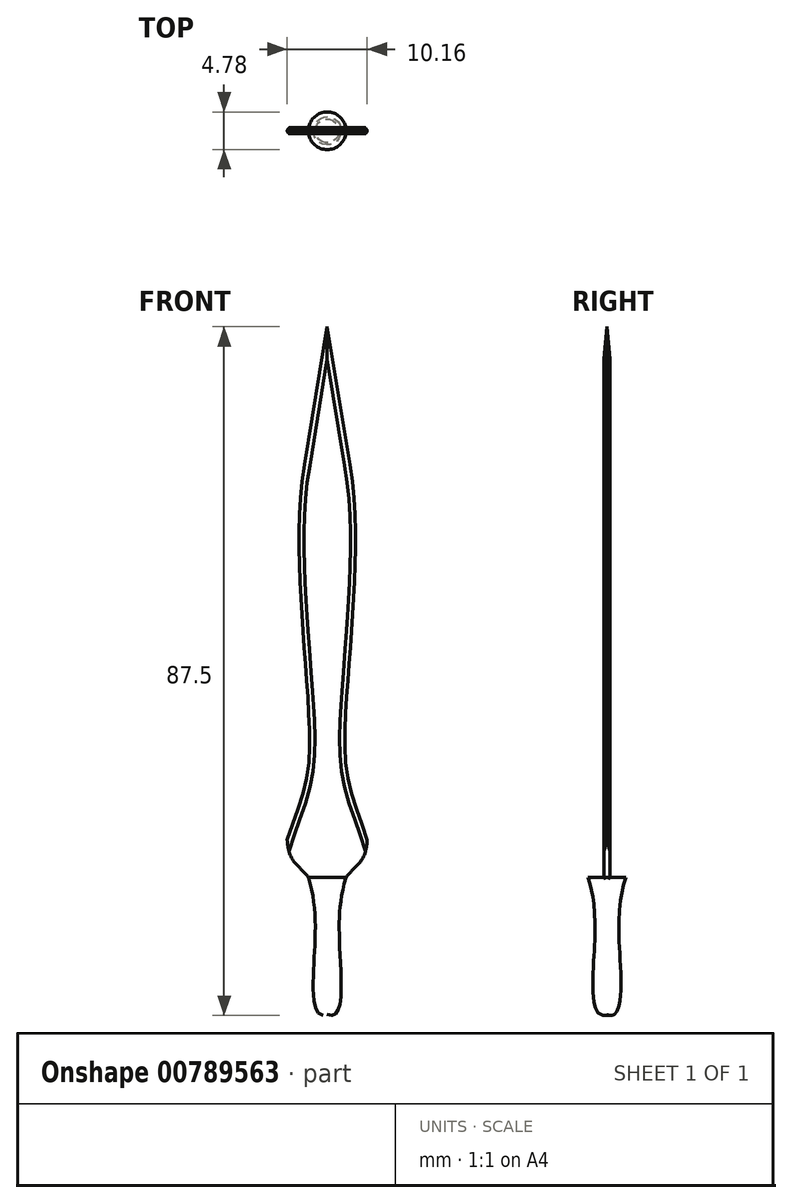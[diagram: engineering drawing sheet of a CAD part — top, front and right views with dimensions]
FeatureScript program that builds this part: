
annotation { "Feature Type Name" : "Feature", "Feature Type Description" : "" }
export const myFeature = defineFeature(function(context is Context, id is Id, definition is map)
    precondition{}
    {
        {
            var Q0;
            Q0=qCreatedBy(makeId("Front.planeOp"),FACE);
            var sketch = newSketch(context, id + "F0", { "sketchPlane" : qUnion([Q0])});
            skLineSegment(sketch, "E0", {"start": v(0, -22.19) * mm, "end": v(0, 65.19) * mm});
            skPoint(sketch, "E1", {"position": v(0, 0) * mm});
            skLineSegment(sketch, "E2", {"start": v(0, 65.19) * mm, "end": v(2.86, 47.67) * mm});
            skPoint(sketch, "E3", {"position": v(1.62, -18.97) * mm});
            skPoint(sketch, "E4", {"position": v(5.08, 0) * mm});
            skFitSpline(sketch, "E5", {"points": [v(2.86, 47.67) * mm, v(2.26, 11.25) * mm, v(5.08, 0) * mm], "startDerivative": vector(9.57, -51.1) * mm, "endDerivative": vector(12.53, -39.06) * mm});
            skFitSpline(sketch, "E6", {"points": [v(5.08, 0) * mm, v(2.23, -5.07) * mm, v(1.62, -18.97) * mm, v(0, -22.19) * mm], "startDerivative": vector(-1.76, -33.31) * mm, "endDerivative": vector(-17, 3.2) * mm});
            skLineSegment(sketch, "E7.MirrorCS", {"start": v(0, 65.19) * mm, "end": v(-2.86, 47.67) * mm});
            skFitSpline(sketch, "E8.MirrorCS", {"points": [v(-2.86, 47.67) * mm, v(-2.26, 11.25) * mm, v(-5.08, 0) * mm], "startDerivative": vector(-9.57, -51.1) * mm, "endDerivative": vector(-12.53, -39.06) * mm});
            skFitSpline(sketch, "E9.MirrorCS", {"points": [v(-5.08, 0) * mm, v(-2.23, -5.07) * mm, v(-1.62, -18.97) * mm, v(0, -22.19) * mm], "startDerivative": vector(1.76, -33.31) * mm, "endDerivative": vector(17, 3.2) * mm});
            skSolve(sketch);
        }
        {
            var Q0;
            Q0 = qSketchRegion(id + "F0", true);
            extrude(context, id + "F1", {"entities" : qUnion([Q0]), "endBound" : BoundingType.SYMMETRIC, "depth" : 0.76 * mm, "offsetDistance" : 25.4 * mm});
        }
        {
            var Q0;
            Q0=makeQuery(id+"F1.opExtrude","CAP_EDGE",EDGE,{"disambiguationData":[OSD([sQuery(id+"F0.wireOp",EDGE,"E5")])],"isStart":false});
            var Q1;
            Q1=makeQuery(id+"F1.opExtrude","CAP_EDGE",EDGE,{"disambiguationData":[OSD([sQuery(id+"F0.wireOp",EDGE,"E8.MirrorCS")])],"isStart":false});
            var Q2;
            Q2=makeQuery(id+"F1.opExtrude","CAP_EDGE",EDGE,{"disambiguationData":[OSD([sQuery(id+"F0.wireOp",EDGE,"E8.MirrorCS")])],"isStart":true});
            var Q3;
            Q3=makeQuery(id+"F1.opExtrude","CAP_EDGE",EDGE,{"disambiguationData":[OSD([sQuery(id+"F0.wireOp",EDGE,"E5")])],"isStart":true});
            var Q4;
            Q4=makeQuery(id+"F1.opExtrude","CAP_EDGE",EDGE,{"disambiguationData":[OSD([sQuery(id+"F0.wireOp",EDGE,"E2")])],"isStart":false});
            var Q5;
            Q5=makeQuery(id+"F1.opExtrude","CAP_EDGE",EDGE,{"disambiguationData":[OSD([sQuery(id+"F0.wireOp",EDGE,"E2")])],"isStart":true});
            var Q6;
            Q6=makeQuery(id+"F1.opExtrude","CAP_EDGE",EDGE,{"disambiguationData":[OSD([sQuery(id+"F0.wireOp",EDGE,"E7.MirrorCS")])],"isStart":false});
            var Q7;
            Q7=makeQuery(id+"F1.opExtrude","CAP_EDGE",EDGE,{"disambiguationData":[OSD([sQuery(id+"F0.wireOp",EDGE,"E7.MirrorCS")])],"isStart":true});
            chamfer(context, id + "F2", {"entities" : qUnion([Q0, Q1, Q2, Q3, Q4, Q5, Q6, Q7]), "chamferType" : ChamferType.OFFSET_ANGLE, "width" : 0.38 * mm, "oppositeDirection" : false, "angle" : 60 * degree, "tangentPropagation" : true});
        }
        {
            var Q0;
            Q0=qCreatedBy(makeId("Front.planeOp"),FACE);
            var sketch = newSketch(context, id + "F3", { "sketchPlane" : qUnion([Q0])});
            skPoint(sketch, "E10", {"position": v(2.4, -4.78) * mm});
            skLineSegment(sketch, "E11", {"start": v(2.4, -4.78) * mm, "end": v(0, -4.78) * mm});
            skPoint(sketch, "E12", {"position": v(0, -22.19) * mm});
            skPoint(sketch, "E13", {"position": v(1.68, -15.34) * mm});
            skPoint(sketch, "E14", {"position": v(5.08, 0) * mm});
            skFitSpline(sketch, "E15", {"points": [v(5.08, 0) * mm, v(1.7, -8) * mm, v(1.68, -15.34) * mm, v(0, -22.19) * mm], "startDerivative": vector(-19.86, -23.26) * mm, "endDerivative": vector(-19.68, 8.84) * mm});
            skLineSegment(sketch, "E16", {"start": v(0, -4.78) * mm, "end": v(0, -22.19) * mm});
            skPoint(sketch, "E17.orphan", {"position": v(-2.4, -4.78) * mm});
            skSolve(sketch);
        }
        {
            var Q0;
            Q0 = qSketchRegion(id + "F3", true);
            var Q1;
            Q1=sQuery(id+"F3.wireOp",EDGE,"E16");
            revolve(context, id + "F4", {"operationType" : NewBodyOperationType.ADD, "surfaceOperationType" : NewSurfaceOperationType.NEW, "entities" : qUnion([Q0]), "axis" : qUnion([Q1]), "revolveType" : RevolveType.FULL});
        }
    });
